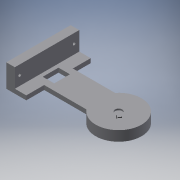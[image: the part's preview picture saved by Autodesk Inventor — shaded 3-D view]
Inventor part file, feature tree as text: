
AUTODESK INVENTOR PART (.ipt)
format: ipt  version: 2017 (Build 210142000, 142)  size: 183,808 bytes
history: native  units: mm
features: extrude x9, sketch x9, other x3, plane x1, hole x1, reference x1
ambient origin geometry x8: Origin, YZ Plane, XZ Plane, XY Plane, X Axis, Y Axis, Z Axis, Center Point
bodies: Solid1 (feature_tree)
feature tree (24):
  extrude  "Extrusion1"  Depth=7.0mm
  extrude  "Extrusion3"  Depth=3.0mm TaperAngle=0.0deg
  sketch  "Sketch5"  dims[d10=45.0mm d11=16.0mm]
  extrude  "Extrusion4"  Depth=16.0mm
  extrude  "Extrusion5"  Depth=3.0mm TaperAngle=0.0deg
  extrude  "Extrusion6"  Depth=8.0mm
  extrude  "Extrusion7"  Depth=2.5mm
  extrude  "Extrusion8"  Depth=11.0mm
  plane  "Work Plane1"
  extrude  "Extrusion11"  Depth=2.0mm
  hole  "Hole1"  [1 undecoded]
  extrude  "Extrusion12"  Depth=5.0mm
  sketch  "Sketch1"  dims[d0=7.0mm d1=0.0mm d6=50.0mm]
  reference  "Reference1"
  sketch  "Sketch4"  dims[d7=10.0mm d8=3.0mm d9=0.0mm]
  sketch  "Sketch6"  dims[d12=16.0mm d13=3.0mm d14=0.0mm]
  sketch  "Sketch7"  dims[d15=3.0mm d16=0.0mm d17=8.0mm]
  sketch  "Sketch8"  dims[d18=13.0mm d19=0.0mm d20=2.5mm]
  sketch  "Sketch12"  dims[d21=8.0mm d22=11.0mm]
  sketch  "Sketch13"  dims[d23=13.0mm d24=0.0mm d25=2.0mm]
  sketch  "Sketch14"  dims[d26=13.0mm d27=0.0mm d35=1.0mm d36=0.0mm d37=3.5mm d38=3.5mm d39=2.0mm d40=6.0mm d41=4.0mm d42=2.0mm d43=90.0deg d44=5.0mm d45=20.594885mm d46=6.0mm d47=14.0mm d48=5.0mm d49=0.0mm]
  other  "<userpath>\Desktop\3d\scanning-robot\Assembly1.iam"
  other  "Assembly1.iam"
  other  "cover:1"
note: 1 required parameter value undecoded (feature->parameter linkage not recoverable at this tier; creation-order binding heuristic only, values carry confidence <= 0.55)
